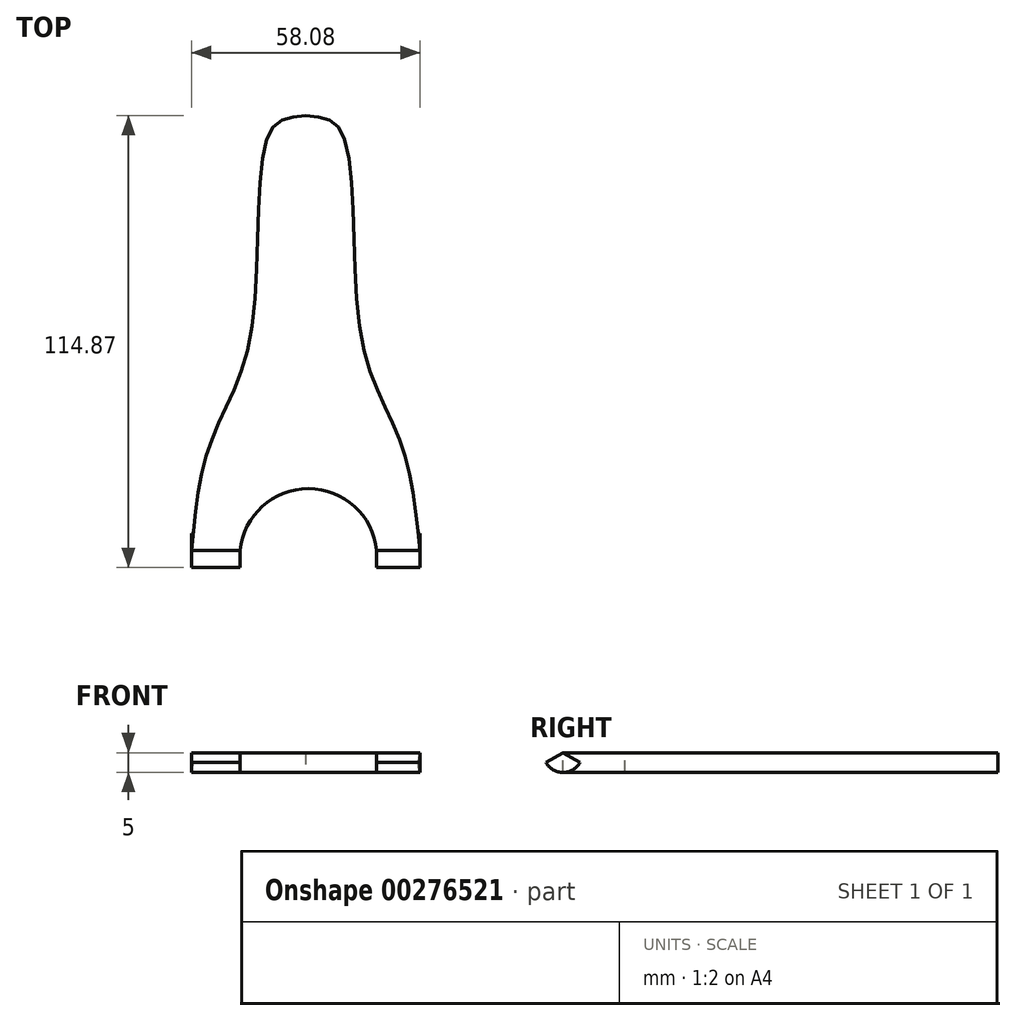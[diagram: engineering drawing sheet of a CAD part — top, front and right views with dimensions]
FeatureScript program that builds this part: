
annotation { "Feature Type Name" : "Feature", "Feature Type Description" : "" }
export const myFeature = defineFeature(function(context is Context, id is Id, definition is map)
    precondition{}
    {
        {
            var Q0;
            Q0=qCreatedBy(makeId("Top.planeOp"),FACE);
            var sketch = newSketch(context, id + "F0", { "sketchPlane" : qUnion([Q0])});
            skFitSpline(sketch, "E0", {"points": [v(0, 55.52) * mm, v(9.13, 51.37) * mm, v(13.94, 0) * mm, v(24.23, -27.8) * mm, v(29.04, -55.02) * mm], "startDerivative": vector(79.44, -6.62) * mm, "endDerivative": vector(11.4, -115.03) * mm});
            skLineSegment(sketch, "E1", {"start": v(29.04, -55.02) * mm, "end": v(0, -55.02) * mm});
            skFitSpline(sketch, "E2.MirrorCS", {"points": [v(0, 55.52) * mm, v(-9.13, 51.37) * mm, v(-13.94, 0) * mm, v(-24.23, -27.8) * mm, v(-29.04, -55.02) * mm], "startDerivative": vector(-79.44, -6.62) * mm, "endDerivative": vector(-11.4, -115.03) * mm});
            skLineSegment(sketch, "E3.MirrorCS", {"start": v(-29.04, -55.02) * mm, "end": v(0, -55.02) * mm});
            skSolve(sketch);
        }
        {
            var Q0;
            Q0 = qSketchRegion(id + "F0", true);
            extrude(context, id + "F1", {"entities" : qUnion([Q0]), "depth" : 5 * mm});
        }
        {
            var Q0;
            Q0=makeQuery(id+"F1.opExtrude","CAP_FACE",FACE,{"disambiguationData":[OSD([sQuery(id+"F0.wireOp",EDGE,"E0"),sQuery(id+"F0.wireOp",EDGE,"E1"),sQuery(id+"F0.wireOp",EDGE,"E2.MirrorCS"),sQuery(id+"F0.wireOp",EDGE,"E3.MirrorCS")])],"isStart":false});
            var sketch = newSketch(context, id + "F2", { "sketchPlane" : qUnion([Q0])});
            skArc(sketch, "E4", {"start": v(18.04, -55.02) * mm, "mid": v(0.7, -39.25) * mm, "end": v(-16.64, -55.02) * mm});
            skSolve(sketch);
        }
        {
            var Q0;
            {var subQ0=sQuery(id+"F2.wireOp",EDGE,"E4");Q0=makeQuery(id+"F2.imprint","IMPRINT",FACE,{"disambiguationData":[TD([[makeQuery(id+"F2.imprint","IMPRINT",EDGE,{"derivedFrom":subQ0}),1.0]])]});}
            extrude(context, id + "F3", {"entities" : qUnion([Q0]), "operationType" : NewBodyOperationType.REMOVE, "oppositeDirection" : true, "depth" : 25 * mm});
        }
        {
            var Q0;
            Q0=qCreatedBy(makeId("Right.planeOp"),FACE);
            var sketch = newSketch(context, id + "F4", { "sketchPlane" : qUnion([Q0])});
            skArc(sketch, "E5", {"start": v(-54.15, 12.56) * mm, "mid": v(-58.64, 9.28) * mm, "end": v(-55.16, 4.95) * mm});
            skSolve(sketch);
        }
        {
            var Q0;
            Q0 = qSketchRegion(id + "F4", true);
            var Q1;
            {var subQ0=sQuery(id+"F0.wireOp",EDGE,"E3.MirrorCS");var subQ1=sQuery(id+"F0.wireOp",EDGE,"E2.MirrorCS");var subQ2=sQuery(id+"F0.wireOp",EDGE,"E1");Q1=makeQuery(id+"F3.boolean.opBoolean","SPLIT",FACE,{"disambiguationData":[TD([makeQuery(id+"F1.opExtrude","SWEPT_FACE",FACE,{"disambiguationData":[OSD([subQ1])]})])],"derivedFrom":makeQuery(id+"F1.opExtrude","SWEPT_FACE",FACE,{"disambiguationData":[OSD([subQ2,subQ0])]})});}
            var Q2;
            {var subQ0=sQuery(id+"F0.wireOp",EDGE,"E0");var subQ1=sQuery(id+"F0.wireOp",EDGE,"E3.MirrorCS");var subQ3=sQuery(id+"F0.wireOp",EDGE,"E1");Q2=makeQuery(id+"F3.boolean.opBoolean","SPLIT",FACE,{"disambiguationData":[TD([makeQuery(id+"F1.opExtrude","SWEPT_FACE",FACE,{"disambiguationData":[OSD([subQ0])]})])],"derivedFrom":makeQuery(id+"F1.opExtrude","SWEPT_FACE",FACE,{"disambiguationData":[OSD([subQ3,subQ1])]})});}
            var Q3;
            {var subQ0=sQuery(id+"F0.wireOp",EDGE,"E3.MirrorCS");var subQ1=sQuery(id+"F0.wireOp",EDGE,"E2.MirrorCS");var subQ2=sQuery(id+"F0.wireOp",EDGE,"E1");Q3=makeQuery(id+"F3.boolean.opBoolean","SPLIT",EDGE,{"disambiguationData":[TD([makeQuery(id+"F1.opExtrude","SWEPT_FACE",FACE,{"disambiguationData":[OSD([subQ1])]})])],"derivedFrom":makeQuery(id+"F1.opExtrude","CAP_EDGE",EDGE,{"disambiguationData":[OSD([subQ2,subQ0])],"isStart":false})});}
            revolve(context, id + "F5", {"operationType" : NewBodyOperationType.ADD, "entities" : qUnion([Q0, Q1, Q2]), "axis" : qUnion([Q3]), "revolveType" : RevolveType.SYMMETRIC, "angle" : 120 * degree});
        }
    });
